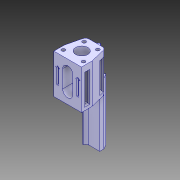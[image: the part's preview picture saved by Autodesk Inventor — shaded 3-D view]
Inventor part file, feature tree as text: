
AUTODESK INVENTOR PART (.ipt)
format: ipt  version: 2018 (Build 220112000, 112)  size: 506,880 bytes
history: native  units: mm
features: other x20, extrude x10, sketch x9
ambient origin geometry x8: Origin, YZ Plane, XZ Plane, XY Plane, X Axis, Y Axis, Z Axis, Center Point
bodies: Body1 (feature_tree), Body2 (feature_tree)
feature tree (39):
  other  "Sólido1"
  extrude  "Extrusión1"  Depth=3.0mm
  other  "Edición directa3"
  other  "Edición directa4"
  extrude  "Extrusión2"  Depth=3.0mm
  extrude  "Extrusión3"  TaperAngle=0.0deg  [1 undecoded]
  extrude  "Extrusión7"  TaperAngle=0.0deg  [1 undecoded]
  extrude  "Extrusión8"  Depth=7.0mm
  extrude  "Extrusión9"  Depth=7.0mm
  extrude  "Extrusión10"  Depth=7.0mm
  other  "Edición directa7"
  other  "Edición directa8"
  extrude  "Extrusión13"  Depth=1.0mm
  other  "Edición directa10"
  other  "Edición directa11"
  extrude  "Extrusión14"  Depth=10.0mm
  extrude  "Extrusión15"  Depth=10.0mm
  other  "Edición directa12"
  other  "Edición directa13"
  sketch  "Boceto1"  dims[d6=3.0mm d7=3.0mm]
  sketch  "Boceto2"  dims[d8=3.0mm d9=3.0mm]
  sketch  "Boceto4"  dims[d10=3.0mm d11=0.0mm d15=0.0mm d16=0.0mm d17=-2.5mm]
  sketch  "Boceto8"  dims[d18=0.0mm d19=0.0mm d20=-2.5mm d21=0.0mm d22=0.0mm d23=-1.5mm]
  sketch  "Boceto9"  dims[d24=0.0mm d25=0.0mm d26=-2.0mm d27=7.0mm]
  sketch  "Boceto10"  dims[d28=7.0mm d29=7.0mm]
  sketch  "Boceto15"  dims[d30=7.0mm d31=7.0mm]
  sketch  "Boceto16"  dims[d32=0.0mm d33=1.0mm]
  sketch  "Boceto17"  dims[d34=1.0mm d35=4.0mm d36=3.0mm d37=1.5mm d39=1.5mm d40=1.5mm d41=0.0mm d42=10.0mm d57=40.0mm d58=60.0deg d59=3.0mm d60=50.0mm d61=60.0deg d62=35.0mm d63=0.0mm d64=15.0mm d65=30.0deg d66=3.0mm d67=25.0mm d68=0.0mm d69=33.0mm d70=30.0mm d71=4.0mm d72=3.0mm d73=0.0mm d77=55.0mm d78=0.0mm d91=0.0mm d92=0.0mm d93=20.0mm d97=0.0mm d98=0.0mm d99=10.0mm d103=15.0mm d104=0.0mm d105=0.0mm d106=0.0mm d107=3.0mm d108=0.0mm d109=0.0mm d110=10.0mm d111=15.0mm d112=90.0deg d113=15.0mm d114=9.5mm d115=0.0mm d120=4.2mm d121=4.2mm d123=10.0mm d126=10.0mm d127=11.0mm d128=0.0mm d129=0.0mm d130=-5.0mm d131=0.0mm d132=0.0mm d133=0.0mm d134=5.0mm]
  other  "PartBody"
  other  "Desplazar4"
  other  "Desplazar5"
  other  "Desplazar6"
  other  "Desplazar7"
  other  "Desplazar11"
  other  "Desplazar13"
  other  "Desplazar15"
  other  "Desplazar16"
  other  "Desplazar17"
  other  "Desplazar18"
note: 2 required parameter values undecoded (feature->parameter linkage not recoverable at this tier; creation-order binding heuristic only, values carry confidence <= 0.55)
